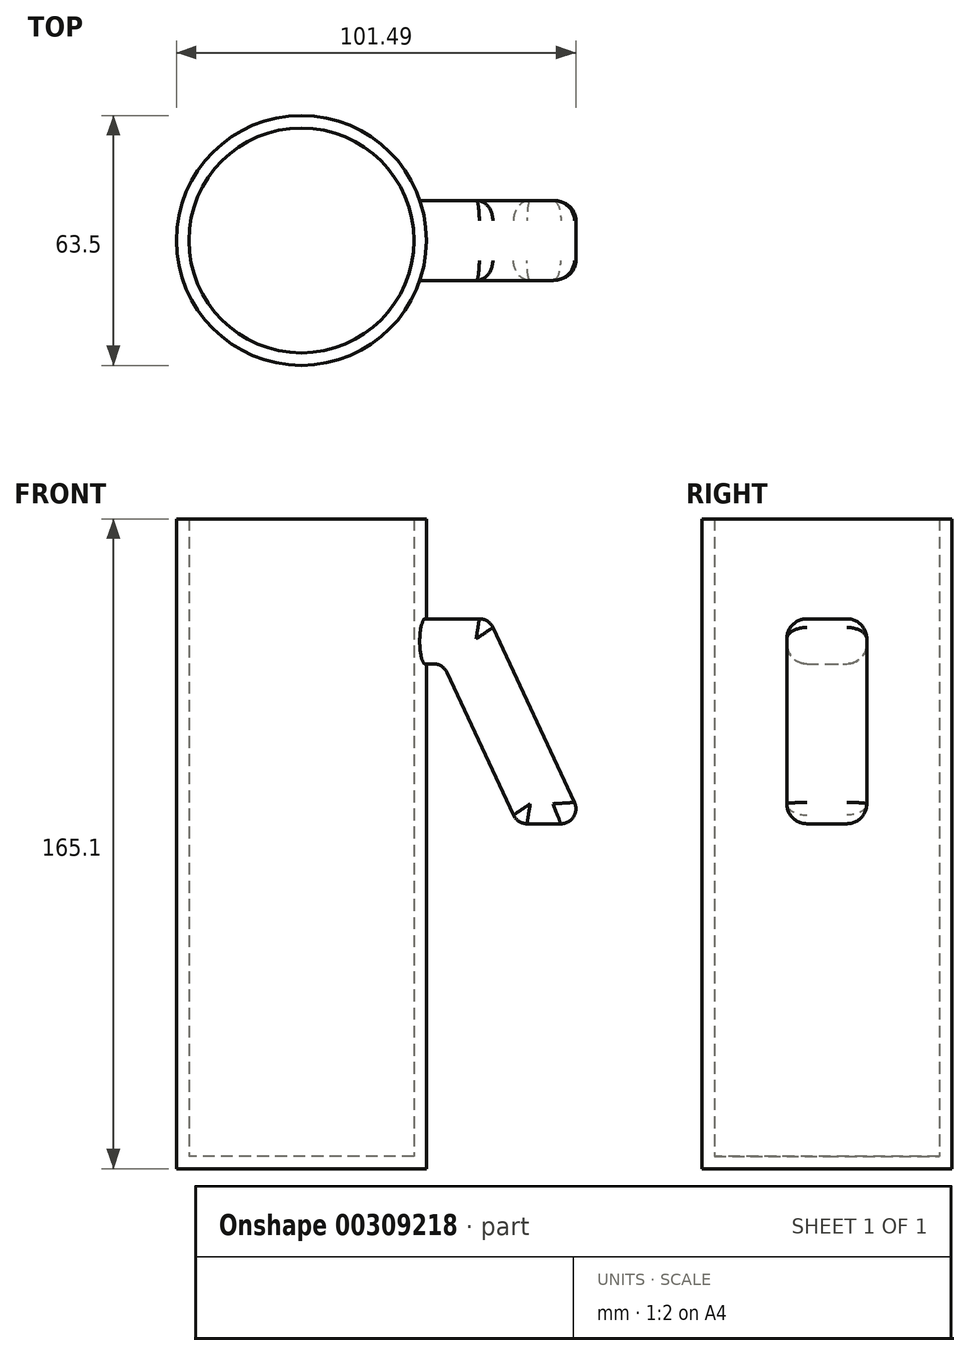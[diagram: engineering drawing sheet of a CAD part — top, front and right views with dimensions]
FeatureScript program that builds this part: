
annotation { "Feature Type Name" : "Feature", "Feature Type Description" : "" }
export const myFeature = defineFeature(function(context is Context, id is Id, definition is map)
    precondition{}
    {
        {
            var Q0;
            Q0=qCreatedBy(makeId("Top.planeOp"),FACE);
            var sketch = newSketch(context, id + "F0", { "sketchPlane" : qUnion([Q0])});
            skCircle(sketch, "E0", {"center": v(0, 0) * mm, "radius": 31.75 * mm});
            skCircle(sketch, "E1", {"center": v(0, 0) * mm, "radius": 28.58 * mm});
            skLineSegment(sketch, "E2", {"start": v(30.08, 10.15) * mm, "end": v(42.15, 10.15) * mm});
            skLineSegment(sketch, "E3", {"start": v(30.08, -10.17) * mm, "end": v(42.14, -10.17) * mm});
            skLineSegment(sketch, "E4", {"start": v(45.96, 6.34) * mm, "end": v(45.95, -6.36) * mm});
            skPoint(sketch, "E5.visualSharp", {"position": v(45.96, 10.15) * mm});
            skArc(sketch, "E5.filletArc", {"start": v(45.96, 6.34) * mm, "mid": v(44.84, 9.03) * mm, "end": v(42.15, 10.15) * mm});
            skPoint(sketch, "E6.visualSharp", {"position": v(45.95, -10.17) * mm});
            skArc(sketch, "E6.filletArc", {"start": v(42.14, -10.17) * mm, "mid": v(44.84, -9.06) * mm, "end": v(45.95, -6.36) * mm});
            skSolve(sketch);
        }
        {
            var Q0;
            Q0=makeQuery(id+"F0.imprint","IMPRINT",FACE,{"disambiguationData":[TD([[makeQuery(id+"F0.imprint","IMPRINT",EDGE,{"derivedFrom":sQuery(id+"F0.wireOp",EDGE,"E1")}),-1.0]])]});
            extrude(context, id + "F1", {"entities" : qUnion([Q0]), "depth" : 165.1 * mm});
        }
        {
            var Q0;
            Q0=qCreatedBy(makeId("Top.planeOp"),FACE);
            var sketch = newSketch(context, id + "F2", { "sketchPlane" : qUnion([Q0])});
            skCircle(sketch, "E7", {"center": v(0, 0) * mm, "radius": 31.75 * mm});
            skSolve(sketch);
        }
        {
            var Q0;
            Q0 = qSketchRegion(id + "F2", true);
            extrude(context, id + "F3", {"entities" : qUnion([Q0]), "operationType" : NewBodyOperationType.ADD, "depth" : 3.17 * mm});
        }
        {
            var Q0;
            Q0=qCreatedBy(makeId("Front.planeOp"),FACE);
            var sketch = newSketch(context, id + "F4", { "sketchPlane" : qUnion([Q0])});
            skLineSegment(sketch, "E8.0", {"start": v(-31.75, 165.1) * mm, "end": v(31.75, 165.1) * mm});
            skLineSegment(sketch, "E9", {"start": v(28.6, 139.7) * mm, "end": v(31.75, 139.7) * mm});
            skLineSegment(sketch, "E10", {"start": v(31.75, 139.7) * mm, "end": v(45.2, 139.7) * mm});
            skLineSegment(sketch, "E11", {"start": v(31.75, 165.1) * mm, "end": v(31.75, 139.7) * mm});
            skLineSegment(sketch, "E12", {"start": v(48.65, 137.5) * mm, "end": v(69.38, 93.05) * mm});
            skLineSegment(sketch, "E13", {"start": v(28.6, 139.7) * mm, "end": v(28.6, 128.27) * mm});
            skLineSegment(sketch, "E14", {"start": v(28.6, 128.27) * mm, "end": v(33.51, 128.27) * mm});
            skLineSegment(sketch, "E15", {"start": v(36.97, 126.07) * mm, "end": v(53.87, 89.83) * mm});
            skLineSegment(sketch, "E16", {"start": v(57.32, 87.63) * mm, "end": v(65.93, 87.63) * mm});
            skPoint(sketch, "E17.visualSharp", {"position": v(35.94, 128.27) * mm});
            skArc(sketch, "E17.filletArc", {"start": v(36.97, 126.07) * mm, "mid": v(35.56, 127.67) * mm, "end": v(33.51, 128.27) * mm});
            skPoint(sketch, "E18.visualSharp", {"position": v(54.9, 87.63) * mm});
            skArc(sketch, "E18.filletArc", {"start": v(53.87, 89.83) * mm, "mid": v(55.27, 88.23) * mm, "end": v(57.32, 87.63) * mm});
            skPoint(sketch, "E19.visualSharp", {"position": v(71.9, 87.63) * mm});
            skArc(sketch, "E19.filletArc", {"start": v(65.93, 87.63) * mm, "mid": v(69.14, 89.4) * mm, "end": v(69.38, 93.05) * mm});
            skPoint(sketch, "E20.visualSharp", {"position": v(47.63, 139.7) * mm});
            skArc(sketch, "E20.filletArc", {"start": v(48.65, 137.5) * mm, "mid": v(47.24, 139.1) * mm, "end": v(45.2, 139.7) * mm});
            skSolve(sketch);
        }
        {
            var Q0;
            Q0 = qSketchRegion(id + "F4", true);
            extrude(context, id + "F5", {"entities" : qUnion([Q0]), "operationType" : NewBodyOperationType.ADD, "depth" : 20.32 * mm, "symmetric" : true});
        }
        {
            var Q0;
            Q0=makeQuery(id+"F5.opExtrude","CAP_EDGE",EDGE,{"disambiguationData":[OSD([sQuery(id+"F4.wireOp",EDGE,"E15")])],"isStart":false});
            fillet(context, id + "F6", {"entities" : qUnion([Q0]), "radius" : 5.08 * mm, "tangentPropagation" : true, "allowEdgeOverflow" : false});
        }
        {
            var Q0;
            Q0=makeQuery(id+"F5.opExtrude","CAP_EDGE",EDGE,{"disambiguationData":[OSD([sQuery(id+"F4.wireOp",EDGE,"E15")])],"isStart":true});
            fillet(context, id + "F7", {"entities" : qUnion([Q0]), "radius" : 5.08 * mm, "tangentPropagation" : true, "allowEdgeOverflow" : false});
        }
    });
